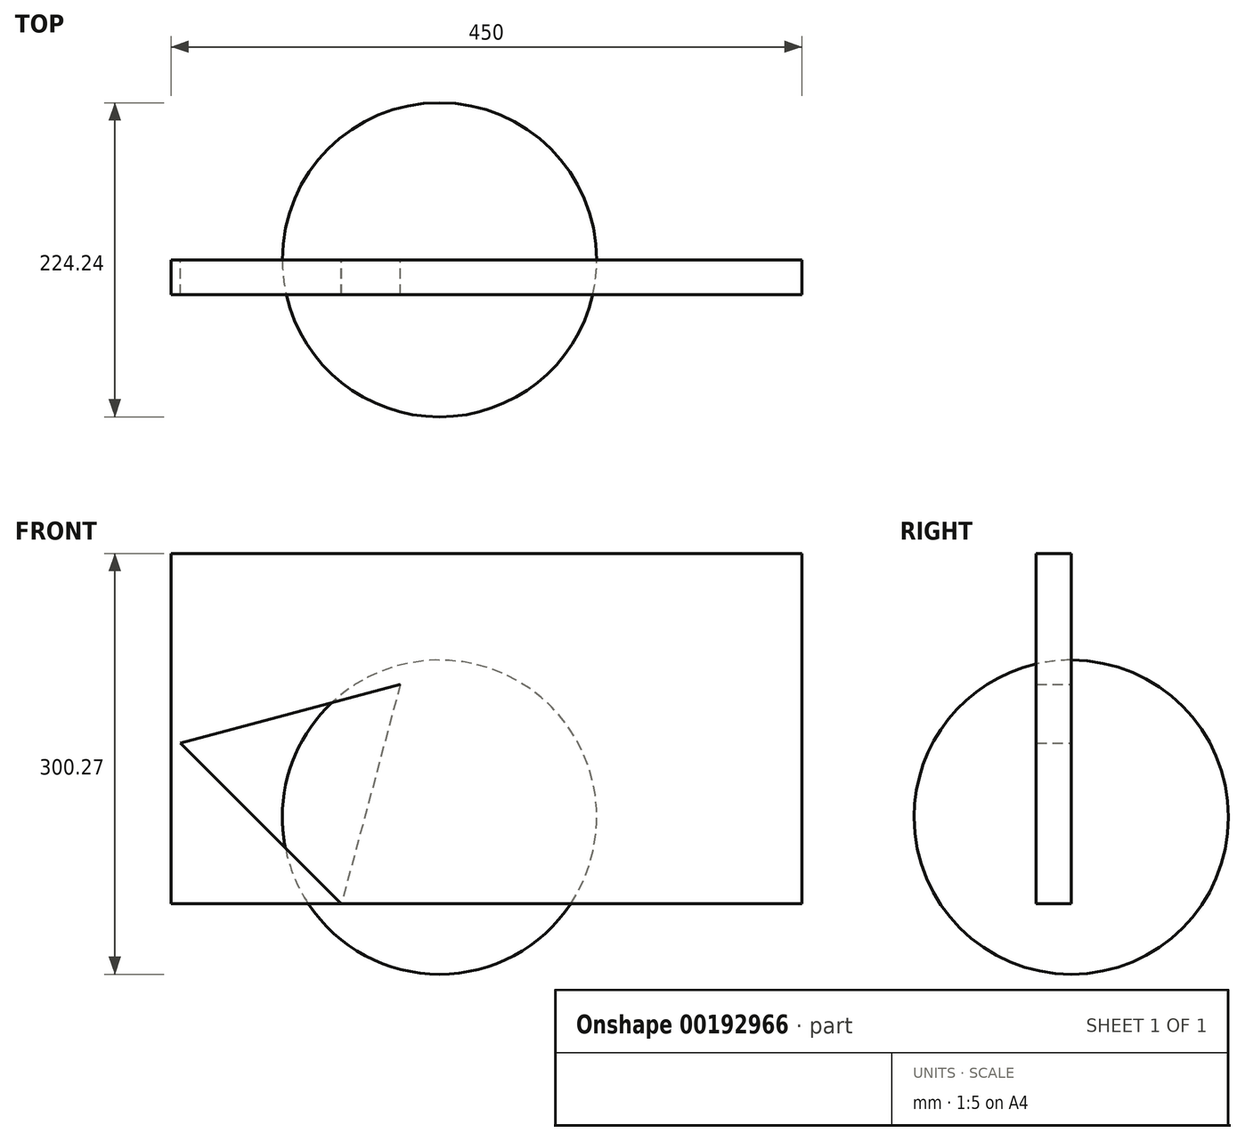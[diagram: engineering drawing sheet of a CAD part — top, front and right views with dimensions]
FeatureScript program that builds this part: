
annotation { "Feature Type Name" : "Feature", "Feature Type Description" : "" }
export const myFeature = defineFeature(function(context is Context, id is Id, definition is map)
    precondition{}
    {
        {
            var Q0;
            Q0=qCreatedBy(makeId("Front.planeOp"),FACE);
            var sketch = newSketch(context, id + "F0", { "sketchPlane" : qUnion([Q0])});
            skLineSegment(sketch, "E0.bottom", {"start": v(-191.54, -61.85) * mm, "end": v(258.46, -61.85) * mm});
            skLineSegment(sketch, "E0.top", {"start": v(-191.54, 188.15) * mm, "end": v(258.46, 188.15) * mm});
            skLineSegment(sketch, "E0.left", {"start": v(-191.54, -61.85) * mm, "end": v(-191.54, 188.15) * mm});
            skLineSegment(sketch, "E0.right", {"start": v(258.46, -61.85) * mm, "end": v(258.46, 188.15) * mm});
            skSolve(sketch);
        }
        {
            var Q0;
            Q0=makeQuery(id+"F0.imprint","IMPRINT",FACE,{"disambiguationData":[TD([[makeQuery(id+"F0.imprint","IMPRINT",EDGE,{"derivedFrom":sQuery(id+"F0.wireOp",EDGE,"E0.bottom")}),1.0]])]});
            extrude(context, id + "F1", {"entities" : qUnion([Q0]), "depth" : 25 * mm});
        }
        {
            var Q0;
            Q0=makeQuery(id+"F1.opExtrude","CAP_FACE",FACE,{"disambiguationData":[OSD([sQuery(id+"F0.wireOp",EDGE,"E0.bottom"),sQuery(id+"F0.wireOp",EDGE,"E0.top"),sQuery(id+"F0.wireOp",EDGE,"E0.left"),sQuery(id+"F0.wireOp",EDGE,"E0.right")])],"isStart":true});
            var sketch = newSketch(context, id + "F2", { "sketchPlane" : qUnion([Q0])});
            skCircle(sketch, "E1.cCircle", {"center": v(94.25, 28.54) * mm, "radius": 46.88 * mm, "construction": true});
            skLineSegment(sketch, "E1.0", {"start": v(184.81, 52.8) * mm, "end": v(69.99, -62.02) * mm});
            skLineSegment(sketch, "E1.1", {"start": v(69.99, -62.02) * mm, "end": v(27.96, 94.83) * mm});
            skLineSegment(sketch, "E1.2", {"start": v(27.96, 94.83) * mm, "end": v(184.81, 52.8) * mm});
            skPoint(sketch, "E1.0.midPoint", {"position": v(127.4, -4.6) * mm});
            skSolve(sketch);
        }
        {
            var Q0;
            {var subQ0=sQuery(id+"F2.wireOp",EDGE,"E1.2");Q0=makeQuery(id+"F2.imprint","IMPRINT",FACE,{"disambiguationData":[TD([[makeQuery(id+"F2.imprint","IMPRINT",EDGE,{"derivedFrom":subQ0}),-1.0]])]});}
            extrude(context, id + "F3", {"entities" : qUnion([Q0]), "operationType" : NewBodyOperationType.REMOVE, "oppositeDirection" : true, "depth" : 50 * mm});
        }
        {
            var Q0;
            Q0=qCreatedBy(makeId("Top.planeOp"),FACE);
            var sketch = newSketch(context, id + "F4", { "sketchPlane" : qUnion([Q0])});
            skArc(sketch, "E2", {"start": v(0, 112.12) * mm, "mid": v(-112.12, 0) * mm, "end": v(0, -112.12) * mm});
            skLineSegment(sketch, "E3", {"start": v(0, 0) * mm, "end": v(0, -112.12) * mm});
            skLineSegment(sketch, "E4.MirrorCS", {"start": v(0, 0) * mm, "end": v(0, 112.12) * mm});
            skSolve(sketch);
        }
        {
            var Q0;
            Q0=makeQuery(id+"F4.imprint","IMPRINT",FACE,{"disambiguationData":[TD([[makeQuery(id+"F4.imprint","IMPRINT",EDGE,{"derivedFrom":sQuery(id+"F4.wireOp",EDGE,"E2")}),1.0]])]});
            var Q1;
            Q1=sQuery(id+"F4.wireOp",EDGE,"E3");
            revolve(context, id + "F5", {"entities" : qUnion([Q0]), "axis" : qUnion([Q1]), "revolveType" : RevolveType.FULL});
        }
    });
